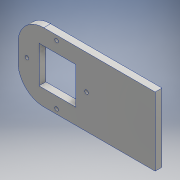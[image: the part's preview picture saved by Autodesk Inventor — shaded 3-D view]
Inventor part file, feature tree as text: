
AUTODESK INVENTOR PART (.ipt)
format: ipt  version: 2016 (Build 200138000, 138)  size: 140,288 bytes
history: native  units: mm
features: extrude x3, sketch x3, fillet x2, other x1
ambient origin geometry x8: Origin, YZ Plane, XZ Plane, XY Plane, X Axis, Y Axis, Z Axis, Center Point
bodies: Body1 (feature_tree)
feature tree (9):
  other  "ソリッド1"
  extrude  "押し出し1"  Depth=160.0mm
  extrude  "押し出し2"  Depth=80.0mm
  extrude  "押し出し3"  Depth=8.0mm TaperAngle=0.0deg
  fillet  "フィレット1"  Radius=43.0mm
  fillet  "フィレット2"  Radius=43.0mm
  sketch  "スケッチ1"
  sketch  "スケッチ2"
  sketch  "スケッチ3"
